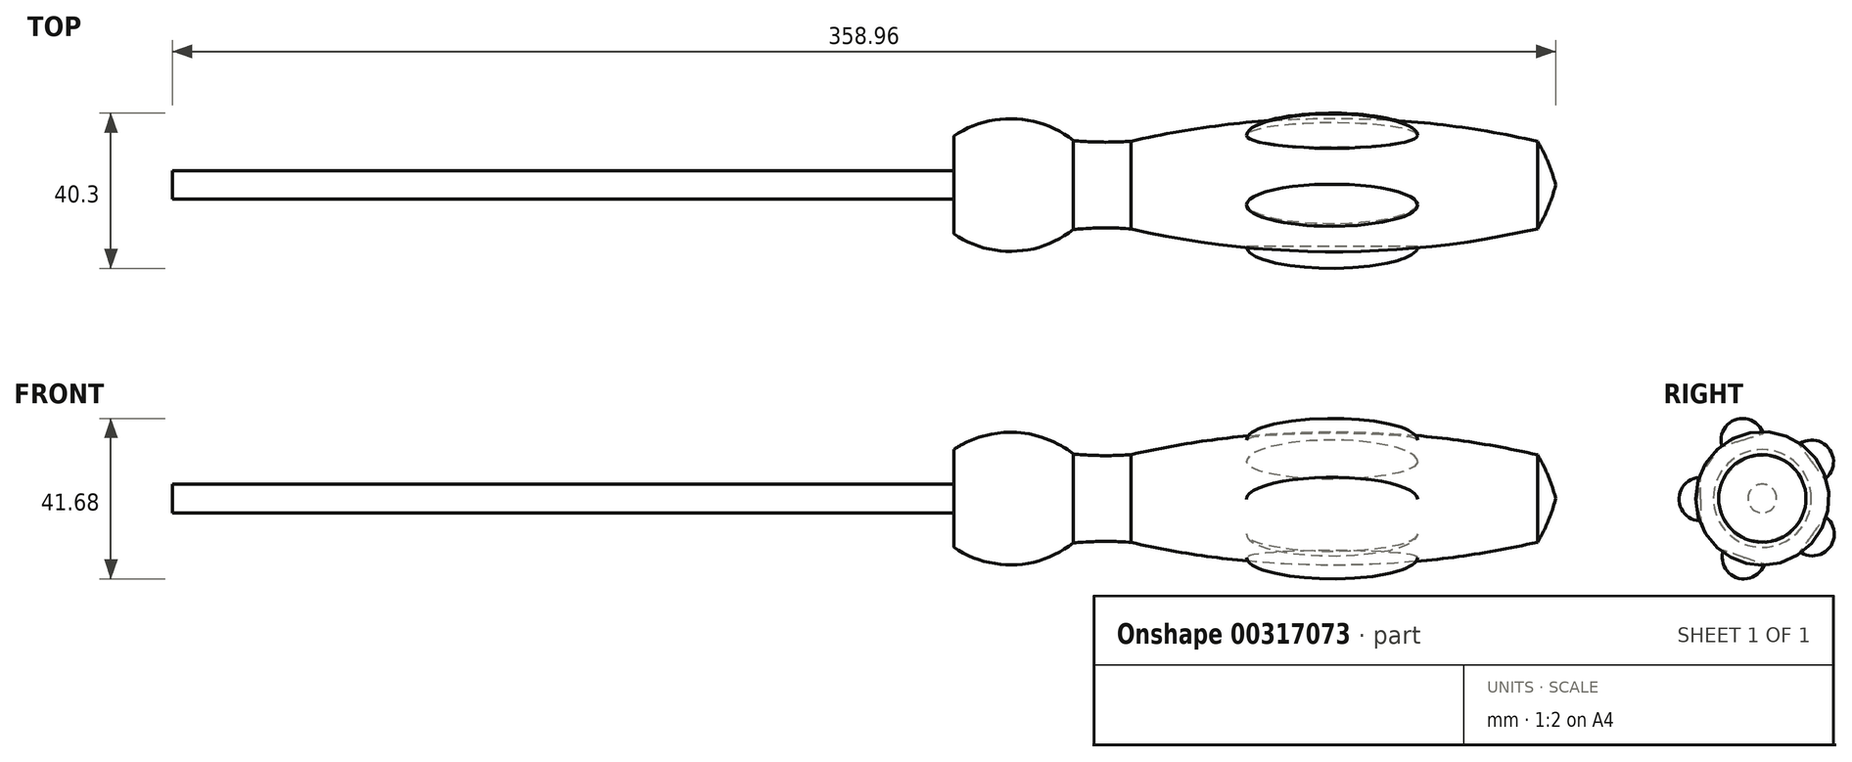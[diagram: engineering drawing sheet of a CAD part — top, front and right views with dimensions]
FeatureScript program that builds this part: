
annotation { "Feature Type Name" : "Feature", "Feature Type Description" : "" }
export const myFeature = defineFeature(function(context is Context, id is Id, definition is map)
    precondition{}
    {
        {
            var Q0;
            Q0=qCreatedBy(makeId("Front.planeOp"),FACE);
            var sketch = newSketch(context, id + "F0", { "sketchPlane" : qUnion([Q0])});
            skLineSegment(sketch, "E0.bottom", {"start": v(175.5, 1.86) * mm, "end": v(-167.16, 1.86) * mm});
            skLineSegment(sketch, "E0.top", {"start": v(175.5, -1.86) * mm, "end": v(-178.75, -1.86) * mm});
            skPoint(sketch, "E0.middle", {"position": v(0, 0) * mm});
            skLineSegment(sketch, "E1.bottom", {"start": v(23.96, -1.86) * mm, "end": v(175.5, -1.86) * mm});
            skLineSegment(sketch, "E1.left", {"start": v(23.96, -1.86) * mm, "end": v(23.96, 10.84) * mm});
            skArc(sketch, "E2", {"start": v(55, 9.7) * mm, "mid": v(39.67, 15.36) * mm, "end": v(23.96, 10.84) * mm});
            skArc(sketch, "E3", {"start": v(55, 9.7) * mm, "mid": v(62.47, 9.3) * mm, "end": v(69.95, 9.54) * mm});
            skArc(sketch, "E4", {"start": v(175.5, 9.49) * mm, "mid": v(122.72, 15.47) * mm, "end": v(69.95, 9.54) * mm});
            skLineSegment(sketch, "E5", {"start": v(175.5, 9.49) * mm, "end": v(175.5, -1.86) * mm});
            skPoint(sketch, "E6.orphan", {"position": v(178.75, 9.49) * mm});
            skPoint(sketch, "E0.left.start.orphan", {"position": v(178.75, 1.86) * mm});
            skPoint(sketch, "E7.orphan", {"position": v(178.75, -1.86) * mm});
            skArc(sketch, "E8", {"start": v(180.21, -1.86) * mm, "mid": v(178.27, 3.99) * mm, "end": v(175.5, 9.49) * mm});
            skLineSegment(sketch, "E9", {"start": v(175.5, -1.86) * mm, "end": v(180.21, -1.86) * mm});
            skPoint(sketch, "E10.orphan", {"position": v(175.5, -33.95) * mm});
            skPoint(sketch, "E0.right.start.orphan", {"position": v(-178.75, 1.86) * mm});
            skLineSegment(sketch, "E11", {"start": v(180.21, -1.86) * mm, "end": v(310.04, -1.86) * mm, "construction": true});
            skLineSegment(sketch, "E12", {"start": v(-178.75, -1.86) * mm, "end": v(-178.75, 1.86) * mm});
            skLineSegment(sketch, "E13", {"start": v(-167.16, 1.86) * mm, "end": v(-178.75, 1.86) * mm});
            skSolve(sketch);
        }
        {
            var Q0;
            Q0 = qSketchRegion(id + "F0", true);
            var Q1;
            Q1=sQuery(id+"F0.wireOp",EDGE,"E0.top");
            revolve(context, id + "F1", {"entities" : qUnion([Q0]), "axis" : qUnion([Q1]), "revolveType" : RevolveType.FULL});
        }
        {
            var Q0;
            Q0=qCreatedBy(makeId("Front.planeOp"),FACE);
            cPlane(context, id + "F2", {"entities" : qUnion([Q0]), "cplaneType" : CPlaneType.OFFSET, "offset" : 16 * mm, "width" : 152.4 * mm, "height" : 152.4 * mm});
        }
        {
            var Q0;
            Q0=qCreatedBy(id+"F2.planeOp",FACE);
            var sketch = newSketch(context, id + "F3", { "sketchPlane" : qUnion([Q0])});
            skEllipticalArc(sketch, "E14", {});
            skLineSegment(sketch, "E15", {"start": v(99.94, -2.03) * mm, "end": v(144.4, -2.03) * mm});
            const initialGuessF3  = {"E14": [0.12216648459434509, -0.0020253739785403013, 1, 0, 0.02222454859145033, 0.005624713140686214, 0, 3.141592653589793]};
            skSetInitialGuess(sketch, initialGuessF3);
            skSolve(sketch);
        }
        {
            var Q0;
            Q0 = qSketchRegion(id + "F3", true);
            var Q1;
            Q1=sQuery(id+"F3.wireOp",EDGE,"E15");
            revolve(context, id + "F4", {"entities" : qUnion([Q0]), "axis" : qUnion([Q1]), "revolveType" : RevolveType.ONE_DIRECTION, "angle" : 180 * degree});
        }
        {
            var Q0;
            Q0=makeQuery(id+"F4.opRevolve","SWEPT_BODY",BODY,{"disambiguationData":[OSD([sQuery(id+"F3.wireOp",EDGE,"E14"),sQuery(id+"F3.wireOp",EDGE,"E15")])]});
            var Q1;
            Q1=sQuery(id+"F0.wireOp",EDGE,"E11");
            circularPattern(context, id + "F5", {"entities" : qUnion([Q0]), "axis" : qUnion([Q1]), "angle" : 360 * degree, "instanceCount" : 5, "equalSpace" : true});
        }
    });
